# Revit family: FP_Revit_18_DD60STX6HI1_DishDrawer_90001209A
name_source: partatom
category: Specialty Equipment
revit_build: Autodesk Revit 2018 (Build: 20170223_1515(x64)
units: mm (PartAtom-declared; Revit-internal decimal feet)

## family parameters
Always vertical = Yes
Cut with Voids When Loaded = Yes
OmniClass Number = 23.40.40.14.31
OmniClass Title = Cleaning and Disposal Equipment
Part Type = Normal
Room Calculation Point = No
Round Connector Dimension = Use Diameter
Shared = No
Work Plane-Based = No

## types (2) — shared parameters
Cavity - Depth (excluding front panel) = 560 mm  [stored 1.83727 ft]
Cavity - Width = 600 mm  [stored 1.9685 ft]
Chassis - Depth = 553 mm  [stored 1.8143 ft]
Connector Description - Electrical = 220-240 V, 50 Hz, min 8.5 A, fused electrical supply
Connector Description - Sanitary = Drain Hose, No Fitting Required
Connector Description - Venting = Vent Ducting Kit Provided, refer to instalation guide
Connector Description - Water = 3/4” BSP (GB20) to suit flat washer
Description = 60cm DishDrawer, Integrated
Manufacturer = Fisher & Paykel Appliances
Material - Body = Fisher & Paykel - Grey
Material - Front = Fisher & Paykel - Stainless Steel
Material - Trim = Fisher & Paykel - Black
Product - Depth = 571 mm  [stored 1.87336 ft]
Product - Height = 454 mm  [stored 1.4895 ft]
Product - Width = 599 mm  [stored 1.96522 ft]
URL = www.fisherpaykel.com
Visibility - Clearance Required = Yes
Visibility - Door Panel = No

## type names (no varying parameters)
- DD60STX6I1
- DD60STX6HI1

note: column(s) folded — value = type name in every type: Model

note: [stored X ft] marks values corroborated as IEEE doubles in the binary element streams (Revit-internal decimal feet)

## geometry (parser evidence)
native form markers: Sweep x3
no freeform markers — native parametric forms only
